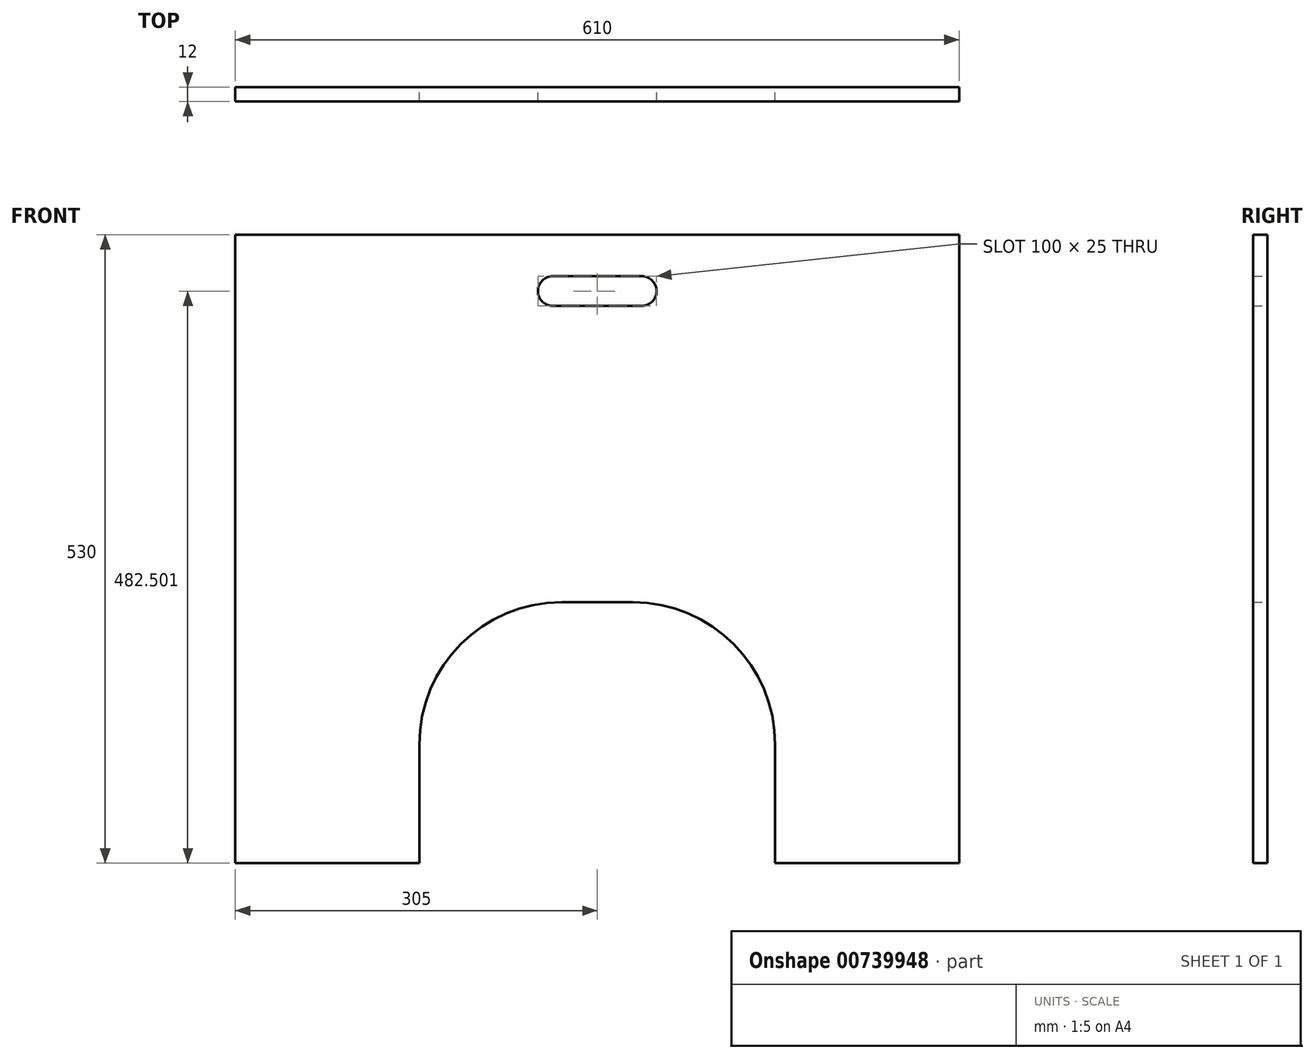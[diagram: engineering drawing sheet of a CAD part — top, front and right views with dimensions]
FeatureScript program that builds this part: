
annotation { "Feature Type Name" : "Feature", "Feature Type Description" : "" }
export const myFeature = defineFeature(function(context is Context, id is Id, definition is map)
    precondition{}
    {
        {
            var Q0;
            Q0=qCreatedBy(makeId("Front.planeOp"),FACE);
            var sketch = newSketch(context, id + "F0", { "sketchPlane" : qUnion([Q0])});
            skLineSegment(sketch, "E0.bottom", {"start": v(305, -256.27) * mm, "end": v(150, -256.27) * mm});
            skLineSegment(sketch, "E0.top", {"start": v(305, 273.73) * mm, "end": v(-305, 273.73) * mm});
            skLineSegment(sketch, "E0.left", {"start": v(305, -256.27) * mm, "end": v(305, 273.73) * mm});
            skLineSegment(sketch, "E0.right", {"start": v(-305, -256.27) * mm, "end": v(-305, 273.73) * mm});
            skPoint(sketch, "E0.middle", {"position": v(0, 8.73) * mm});
            skLineSegment(sketch, "E1.bottom", {"start": v(30, -36.27) * mm, "end": v(-30, -36.27) * mm});
            skLineSegment(sketch, "E1.left", {"start": v(150, -156.27) * mm, "end": v(150, -256.27) * mm});
            skLineSegment(sketch, "E1.right", {"start": v(-150, -156.27) * mm, "end": v(-150, -256.27) * mm});
            skPoint(sketch, "E1.middle", {"position": v(0, -256.27) * mm});
            skPoint(sketch, "E1.top.end.orphan", {"position": v(-150, -476.27) * mm});
            skPoint(sketch, "E2.orphan", {"position": v(150, -476.27) * mm});
            skPoint(sketch, "E3.visualSharp", {"position": v(-150, -36.27) * mm});
            skArc(sketch, "E3.filletArc", {"start": v(-30, -36.27) * mm, "mid": v(-114.85, -71.42) * mm, "end": v(-150, -156.27) * mm});
            skPoint(sketch, "E4.visualSharp", {"position": v(150, -36.27) * mm});
            skArc(sketch, "E4.filletArc", {"start": v(150, -156.27) * mm, "mid": v(114.85, -71.42) * mm, "end": v(30, -36.27) * mm});
            skLineSegment(sketch, "E5.trimOffspring", {"start": v(-150, -256.27) * mm, "end": v(-305, -256.27) * mm});
            skLineSegment(sketch, "E6.bottom", {"start": v(37.5, 238.73) * mm, "end": v(-37.5, 238.73) * mm});
            skLineSegment(sketch, "E6.top", {"start": v(37.5, 213.73) * mm, "end": v(-37.5, 213.73) * mm});
            skPoint(sketch, "E6.middle", {"position": v(0, 226.23) * mm});
            skArc(sketch, "E7", {"start": v(-37.5, 238.73) * mm, "mid": v(-50, 226.23) * mm, "end": v(-37.5, 213.73) * mm});
            skArc(sketch, "E8", {"start": v(37.5, 213.73) * mm, "mid": v(50, 226.23) * mm, "end": v(37.5, 238.73) * mm});
            skSolve(sketch);
        }
        {
            var Q0;
            Q0 = qSketchRegion(id + "F0", true);
            extrude(context, id + "F1", {"entities" : qUnion([Q0]), "depth" : 12 * mm, "offsetDistance" : 25 * mm, "symmetric" : true});
        }
    });
